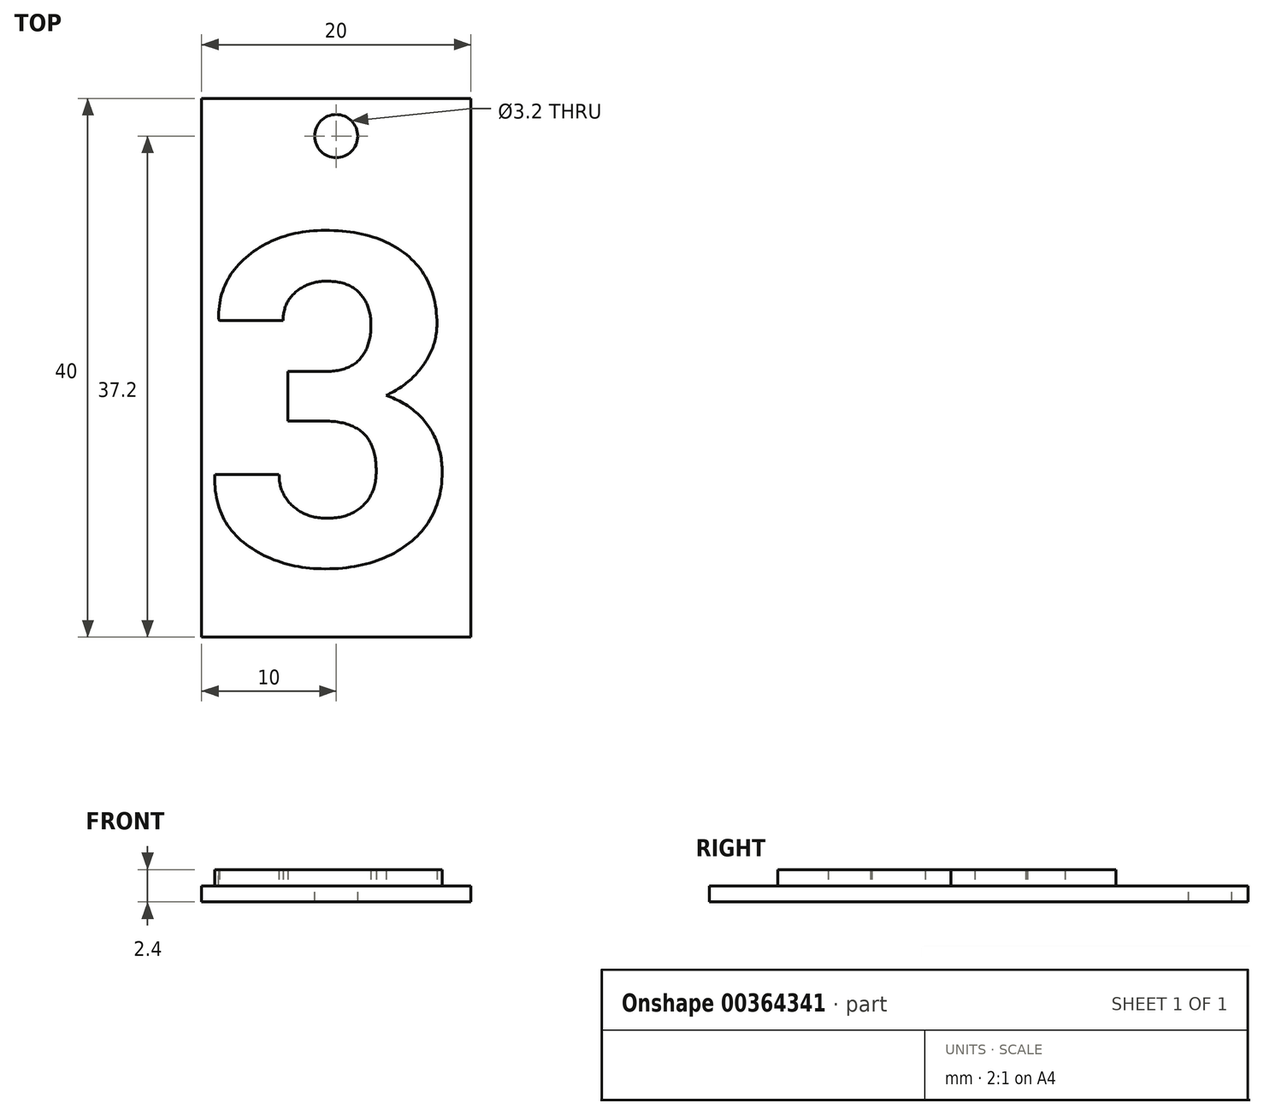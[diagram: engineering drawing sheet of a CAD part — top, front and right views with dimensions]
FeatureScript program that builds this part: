
annotation { "Feature Type Name" : "Feature", "Feature Type Description" : "" }
export const myFeature = defineFeature(function(context is Context, id is Id, definition is map)
    precondition{}
    {
        {
            var Q0;
            Q0=qCreatedBy(makeId("Top.planeOp"),FACE);
            var sketch = newSketch(context, id + "F0", { "sketchPlane" : qUnion([Q0])});
            skLineSegment(sketch, "E0.bottom", {"start": v(10, -20) * mm, "end": v(-10, -20) * mm});
            skLineSegment(sketch, "E0.top", {"start": v(10, 20) * mm, "end": v(-10, 20) * mm});
            skLineSegment(sketch, "E0.left", {"start": v(10, -20) * mm, "end": v(10, 20) * mm});
            skLineSegment(sketch, "E0.right", {"start": v(-10, -20) * mm, "end": v(-10, 20) * mm});
            skPoint(sketch, "E0.middle", {"position": v(0, 0) * mm});
            skCircle(sketch, "E1", {"center": v(0, 17.2) * mm, "radius": 1.6 * mm});
            skLineSegment(sketch, "E2", {"start": v(0, -20) * mm, "end": v(0, 15.6) * mm, "construction": true});
            skLineSegment(sketch, "E3", {"start": v(-10, -2.2) * mm, "end": v(10, -2.2) * mm, "construction": true});
            skPoint(sketch, "E3.startSnap0", {"position": v(0, -2.2) * mm});
            skLineSegment(sketch, "E4", {"start": v(10, -2.2) * mm, "end": v(-10, -2.2) * mm, "construction": true});
            skText(sketch, "E5", { "text": "3", "fontName": "RobotoSlab-Bold.ttf"});
            skLineSegment(sketch, "E6", {"start": v(-9.98, 10.17) * mm, "end": v(9.98, -14.57) * mm, "construction": true});
            skLineSegment(sketch, "E7", {"start": v(9.98, 10.17) * mm, "end": v(-9.98, -14.57) * mm, "construction": true});
            const initialGuessF0  = {"E5": [-0.00998, -0.01457, 1, 0, 0.02473]};
            skSetInitialGuess(sketch, initialGuessF0);
            skSolve(sketch);
        }
        {
            var Q0;
            Q0=makeQuery(id+"F0.imprint","IMPRINT",FACE,{"disambiguationData":[TD([[makeQuery(id+"F0.imprint","IMPRINT",EDGE,{"derivedFrom":sQuery(id+"F0.wireOp",EDGE,"E0.bottom")}),-1.0]])]});
            var Q1;
            Q1=makeQuery(id+"F0.imprint","IMPRINT",FACE,{"disambiguationData":[TD([[makeQuery(id+"F0.imprint","IMPRINT",EDGE,{"derivedFrom":sQuery(id+"F0.wireOp",EDGE,"E5.sketch_text.stroke-0")}),-1.0]])]});
            extrude(context, id + "F1", {"entities" : qUnion([Q0, Q1]), "oppositeDirection" : true, "depth" : 1.2 * mm});
        }
        {
            var Q0;
            Q0=makeQuery(id+"F0.imprint","IMPRINT",FACE,{"disambiguationData":[TD([[makeQuery(id+"F0.imprint","IMPRINT",EDGE,{"derivedFrom":sQuery(id+"F0.wireOp",EDGE,"E5.sketch_text.stroke-0")}),-1.0]])]});
            extrude(context, id + "F2", {"entities" : qUnion([Q0]), "operationType" : NewBodyOperationType.ADD, "depth" : 1.2 * mm});
        }
    });
